# Revit family: Heater-Bromic-Eclipse-Electric-Wall-Mounted2
name_source: partatom
category: Mechanical Equipment
units: mm (PartAtom-declared; Revit-internal decimal feet)

## family parameters
Classification = None
Cut with Voids When Loaded = No
Host = Face
OmniClass Number = 23.75.10.14
OmniClass Title = Independent Electric Heating Units
Part Type = Normal
Room Calculation Point = No
Round Connector Dimension = Use Diameter
Shared = No

## types (1)
- Eclipse Electric - Wall Mounted
    Apparent Load = 2900 VA
    Approximate Heat Area = 121.00 SF
    Default Elevation = 87 "
    Depth = 61 "
    Description = The Eclipse Smart-Heat Electric heater is equipped with 3 different heat outputs up to 2900W and a dimmable LED light railing. Available in six unique mounting options, the Eclipse Smart-Heat™ series adds style, warmth and light to design-focused outdoor spaces.
    Diameter = 28 "
    FloorClearance = 96 "
    Frequency = 60 Hz
    Height = 22 "
    Load Classification = Other
    Load Sub-Classification Motor = No
    Manufacturer = Bromic Heating
    Material = Metal-Steel-Bromic-Black
    Model = Eclipse Smart-Heat™ Electric
    Mounting Type Info = Wall Mounted
    Number of Poles = 1
    Power Factor = 1
    Product data url = https://www.bimobject.com
    ProductCode = BH0920001
    SideClearance = 18 "
    URL = https://www.bromic.com
    Utility = No
    Voltage = 240 V
    Wattage = 2900 W
    calcClearanceFront = 32 "
    calcClearanceWidth = 64 "

## geometry (parser evidence)
native form markers: Sweep x2
no freeform markers — native parametric forms only
